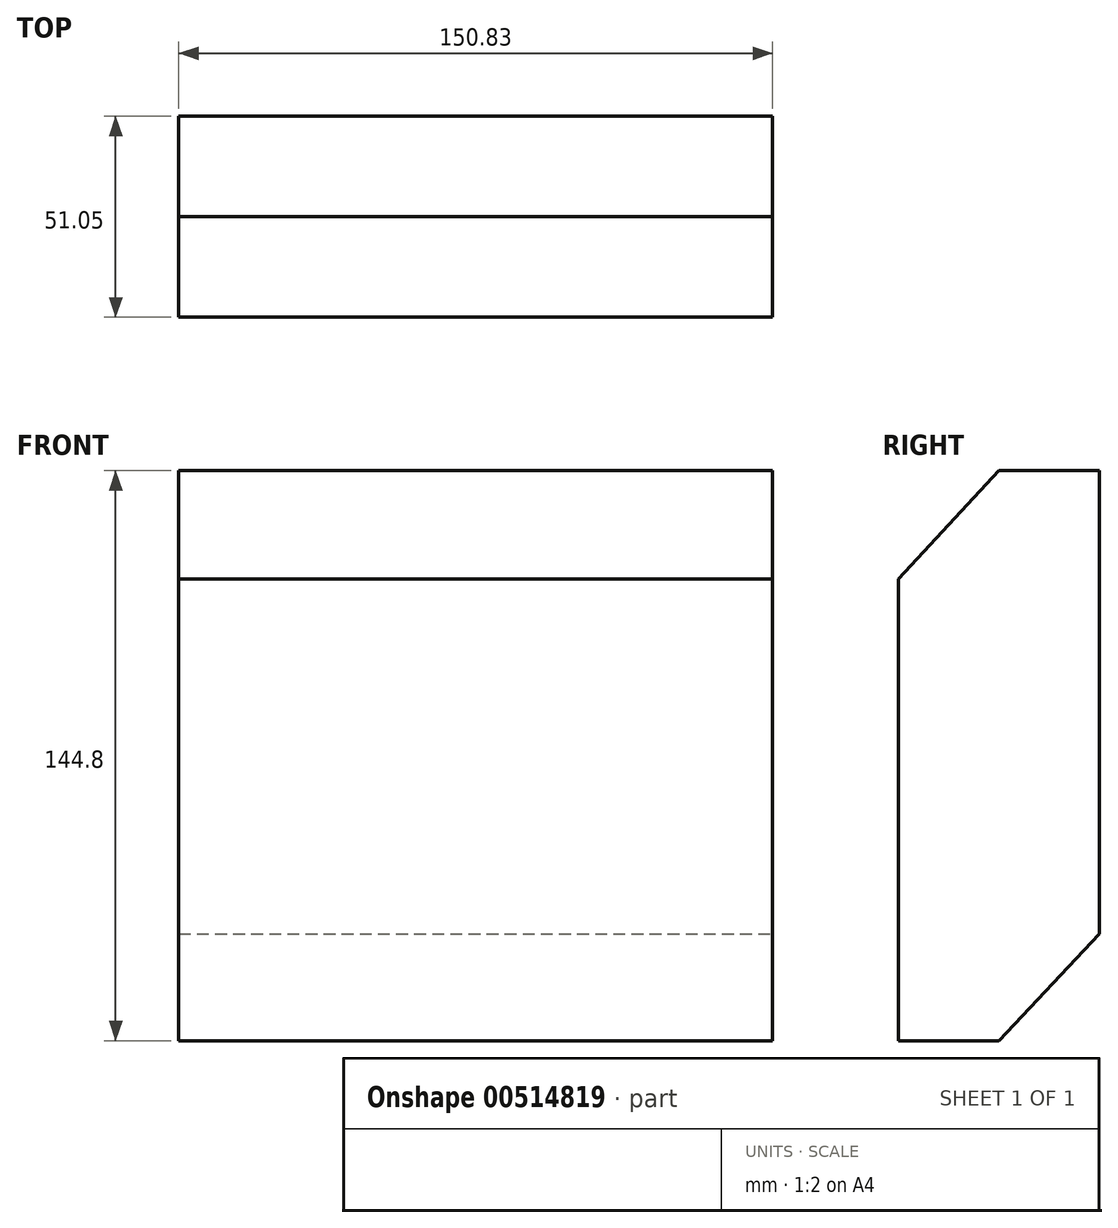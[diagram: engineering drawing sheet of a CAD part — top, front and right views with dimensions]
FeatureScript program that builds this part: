
annotation { "Feature Type Name" : "Feature", "Feature Type Description" : "" }
export const myFeature = defineFeature(function(context is Context, id is Id, definition is map)
    precondition{}
    {
        {
            var Q0;
            Q0=qCreatedBy(makeId("Front.planeOp"),FACE);
            var sketch = newSketch(context, id + "F0", { "sketchPlane" : qUnion([Q0])});
            skLineSegment(sketch, "E0.bottom", {"start": v(-50.49, 53.98) * mm, "end": v(100.34, 53.98) * mm});
            skLineSegment(sketch, "E0.top", {"start": v(-50.49, -90.82) * mm, "end": v(100.34, -90.82) * mm});
            skLineSegment(sketch, "E0.left", {"start": v(-50.49, 53.98) * mm, "end": v(-50.49, -90.82) * mm});
            skLineSegment(sketch, "E0.right", {"start": v(100.34, 53.98) * mm, "end": v(100.34, -90.82) * mm});
            skSolve(sketch);
        }
        {
            var Q0;
            Q0 = qSketchRegion(id + "F0", true);
            extrude(context, id + "F1", {"entities" : qUnion([Q0]), "depth" : 51.05 * mm, "offsetDistance" : 25.4 * mm});
        }
        {
            var Q0;
            Q0=makeQuery(id+"F1.opExtrude","SWEPT_FACE",FACE,{"disambiguationData":[OSD([sQuery(id+"F0.wireOp",EDGE,"E0.right")])]});
            var sketch = newSketch(context, id + "F2", { "sketchPlane" : qUnion([Q0])});
            skLineSegment(sketch, "E1", {"start": v(-51.05, 26.46) * mm, "end": v(-25.53, 53.98) * mm});
            skLineSegment(sketch, "E2", {"start": v(-25.53, 53.98) * mm, "end": v(-51.05, 53.98) * mm});
            skLineSegment(sketch, "E3", {"start": v(-51.05, 53.98) * mm, "end": v(-51.05, 26.46) * mm});
            skLineSegment(sketch, "E4", {"start": v(-25.53, -90.82) * mm, "end": v(0, -63.75) * mm});
            skLineSegment(sketch, "E5", {"start": v(0, -63.75) * mm, "end": v(0, -90.82) * mm});
            skLineSegment(sketch, "E6", {"start": v(0, -90.82) * mm, "end": v(-25.53, -90.82) * mm});
            skSolve(sketch);
        }
        {
            var Q0;
            Q0 = qSketchRegion(id + "F2", true);
            extrude(context, id + "F3", {"entities" : qUnion([Q0]), "operationType" : NewBodyOperationType.REMOVE, "oppositeDirection" : true, "depth" : 160.02 * mm, "offsetDistance" : 25.4 * mm});
        }
    });
